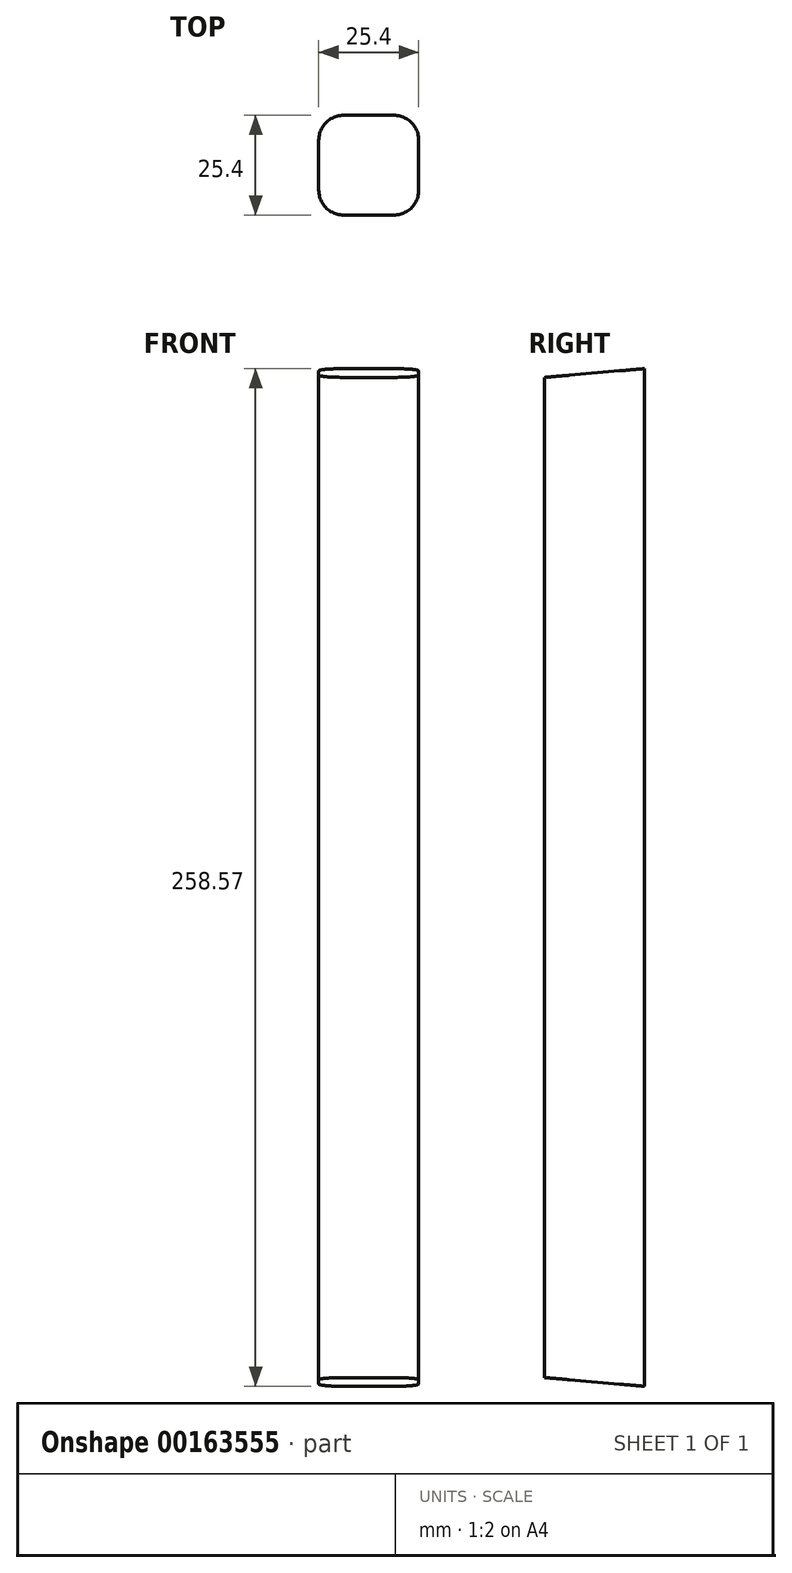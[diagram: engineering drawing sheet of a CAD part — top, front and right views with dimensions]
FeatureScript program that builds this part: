
annotation { "Feature Type Name" : "Feature", "Feature Type Description" : "" }
export const myFeature = defineFeature(function(context is Context, id is Id, definition is map)
    precondition{}
    {
        {
            var Q0;
            Q0=qCreatedBy(makeId("Top.planeOp"),FACE);
            var sketch = newSketch(context, id + "F0", { "sketchPlane" : qUnion([Q0])});
            skLineSegment(sketch, "E0.bottom", {"start": v(6.35, 12.7) * mm, "end": v(-6.35, 12.7) * mm});
            skLineSegment(sketch, "E0.top", {"start": v(6.35, -12.7) * mm, "end": v(-6.35, -12.7) * mm});
            skLineSegment(sketch, "E0.left", {"start": v(12.7, 6.35) * mm, "end": v(12.7, -6.35) * mm});
            skLineSegment(sketch, "E0.right", {"start": v(-12.7, 6.35) * mm, "end": v(-12.7, -6.35) * mm});
            skPoint(sketch, "E0.middle", {"position": v(0, 0) * mm});
            skPoint(sketch, "E1.visualSharp", {"position": v(-12.7, 12.7) * mm});
            skArc(sketch, "E1.filletArc", {"start": v(-6.35, 12.7) * mm, "mid": v(-10.84, 10.84) * mm, "end": v(-12.7, 6.35) * mm});
            skPoint(sketch, "E2.visualSharp", {"position": v(-12.7, -12.7) * mm});
            skArc(sketch, "E2.filletArc", {"start": v(-12.7, -6.35) * mm, "mid": v(-10.84, -10.84) * mm, "end": v(-6.35, -12.7) * mm});
            skPoint(sketch, "E3.visualSharp", {"position": v(12.7, -12.7) * mm});
            skArc(sketch, "E3.filletArc", {"start": v(6.35, -12.7) * mm, "mid": v(10.84, -10.84) * mm, "end": v(12.7, -6.35) * mm});
            skPoint(sketch, "E4.visualSharp", {"position": v(12.7, 12.7) * mm});
            skArc(sketch, "E4.filletArc", {"start": v(12.7, 6.35) * mm, "mid": v(10.84, 10.84) * mm, "end": v(6.35, 12.7) * mm});
            skSolve(sketch);
        }
        {
            var Q0;
            Q0=qSketchRegion(id+"F0",true);
            extrude(context, id + "F1", {"entities" : qUnion([Q0]), "depth" : 258.57 * mm, "offsetDistance" : 25.4 * mm});
        }
        {
            var Q0;
            Q0=qCreatedBy(makeId("Right.planeOp"),FACE);
            var sketch = newSketch(context, id + "F2", { "sketchPlane" : qUnion([Q0])});
            skLineSegment(sketch, "E5", {"start": v(12.7, 0) * mm, "end": v(-17.71, 2.66) * mm});
            skLineSegment(sketch, "E6", {"start": v(-17.71, 2.66) * mm, "end": v(-17.71, 0) * mm});
            skLineSegment(sketch, "E7", {"start": v(-17.71, 0) * mm, "end": v(12.7, 0) * mm});
            skSolve(sketch);
        }
        {
            var Q0;
            Q0=makeQuery(id+"F2.imprint","IMPRINT",FACE,{"disambiguationData":[TD([[makeQuery(id+"F2.imprint","IMPRINT",EDGE,{"derivedFrom":sQuery(id+"F2.wireOp",EDGE,"E5")}),1.0]])]});
            extrude(context, id + "F3", {"entities" : qUnion([Q0]), "operationType" : NewBodyOperationType.REMOVE, "endBound" : BoundingType.SYMMETRIC, "oppositeDirection" : true, "depth" : 25.4 * mm, "offsetDistance" : 25.4 * mm});
        }
        {
            var Q0;
            Q0=qCreatedBy(makeId("Right.planeOp"),FACE);
            var sketch = newSketch(context, id + "F4", { "sketchPlane" : qUnion([Q0])});
            skLineSegment(sketch, "E8", {"start": v(12.7, 258.57) * mm, "end": v(-13.93, 258.57) * mm});
            skLineSegment(sketch, "E9", {"start": v(-13.93, 258.57) * mm, "end": v(-13.93, 256.24) * mm});
            skLineSegment(sketch, "E10", {"start": v(-13.93, 256.24) * mm, "end": v(12.7, 258.57) * mm});
            skSolve(sketch);
        }
        {
            var Q0;
            Q0=qSketchRegion(id+"F4",true);
            extrude(context, id + "F5", {"entities" : qUnion([Q0]), "operationType" : NewBodyOperationType.REMOVE, "endBound" : BoundingType.SYMMETRIC, "oppositeDirection" : true, "depth" : 25.4 * mm, "offsetDistance" : 25.4 * mm});
        }
    });
